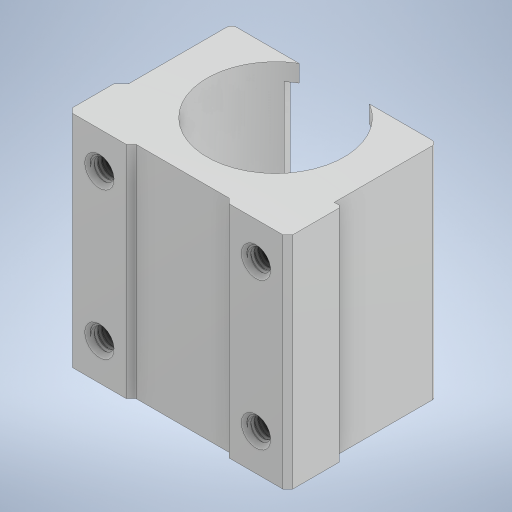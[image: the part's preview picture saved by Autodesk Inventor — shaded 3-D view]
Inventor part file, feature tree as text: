
AUTODESK INVENTOR PART (.ipt)
format: ipt  version: 2024 (Build 280153000, 153)  size: 2,381,312 bytes
history: native  units: in
note: dims shown in document units (in); Inventor stores cm internally (conversion verified against a paired STEP export)
features: extrude x1, sketch x1, other x1
ambient origin geometry x8: Origin, YZ Plane, XZ Plane, XY Plane, X Axis, Y Axis, Z Axis, Center Point
bodies: Solid4 (feature_tree)
feature tree (3):
  extrude  "Extrusion1"  [1 undecoded]
  sketch  "Sketch1"  dims[d0=3.937in d1=0.0in]
  other  "Guide support"
note: 1 required parameter value undecoded (feature->parameter linkage not recoverable at this tier; creation-order binding heuristic only, values carry confidence <= 0.55)
